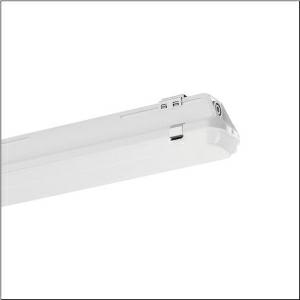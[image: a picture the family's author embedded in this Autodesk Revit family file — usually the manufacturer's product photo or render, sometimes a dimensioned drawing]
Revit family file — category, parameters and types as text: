
# Revit family: monsun_r__12_51fp20mp4b0q_88b3
name_source: partatom
category: Lighting Fixtures
units: mm (PartAtom-declared; Revit-internal decimal feet)

## family parameters
Cut with Voids When Loaded = No
Host = Face
Light Source = No
Part Type = Normal
Room Calculation Point = No
Round Connector Dimension = Use Diameter
Shared = No

## types (1)
- --- (1 x LED, 10910 lm, 66.2 W, 4000K)
    Apparent Load = 66 VA
    CIE Flux Codes = 45 75 93 94 100
    Color Rendering = 80
    Color Temperature = 4000K
    Default Elevation = 1800 mm
    Description = Monsun® 12, damp-proof luminaire, chain hanger, primary optical cover: enclosure, of PC, light emission: direct distribution, primary light characteristic: symmetric, installation type: suspended mounting, surface-mounted, horizontal mounting, vertical mounting, LED rated luminous flux: 10.910 lm, light colour: 840, colour temperature: 4000K, control gear: ECG, with terminal, 3-pole, max. 2.5mm², mains connection: 220..240V, AC, 50/60Hz, rated input power: 66W, luminaire housing, of glass-fibre reinforced polyester, uncoated, bright grey, length: 1.590 mm, width: 90 mm, height: 88mm, clip for enclosure, of stainless steel (V2A), ceiling mounting element, of stainless steel (V2A), chain hanger, of stainless steel (V2A), protection rating (complete): IP66, insulation class (complete): insulation class I (protective earthing), certification: CE, ENEC, VDE, protection symbol: D, impact resistance: IK08, permissible ambient temperature for indoor applications: -35..+35°C, standard: EN 50419, EN 60598-2-1, no direct snow, no direct sun, no direct rain, for indoor or canopied outdoor use, corresponds to IFS (International Featured Standards) requirements for safety and quality in the food industry, packaging unit: 1 piece
    Height = 89 mm
    Lamp = 1 x LED
    Lamp Light Flux = 10910 lm
    Lamp Power = 66.2 W
    Lamp count = 1
    Length = 1590 mm
    Luminous efficacy = 165 lm/W
    Manufacturer = Siteco
    ModVariant = No
    Model = 51FP20MP4B0Q
    Mounting Place = Ceiling
    Mounting Type = Pendant
    Number of Poles = 1
    OnlyDefault = Yes
    Power Factor = 1
    Product Name = Monsun® 12
    Product group = damp-proof luminaire | ceiling pendant
    ProductGroupID = 908
    Protection Class = Protection class I
    Protection Degree = IP 66
    RLX_Detail_Level = 1
    RlxData = <blob elided: 89517 chars, md5=59590ccd>
    Socket = socket
    Standby Power = 0 W
    System Light Flux = 10910 lm
    System Power = 66 W
    Type Comments = factory setting: luminous flux: 100 % | (A | C | E) | 155 mA
    Type Image = l_1004748.jpg
    URL = http://relux.com
    VarID = @adj_133861
    Voltage = 0 V
    Weight = 0.00 kg
    Width = 90 mm

## geometry (parser evidence)
native form markers: Blend x4, Sweep x16
no freeform markers — native parametric forms only
